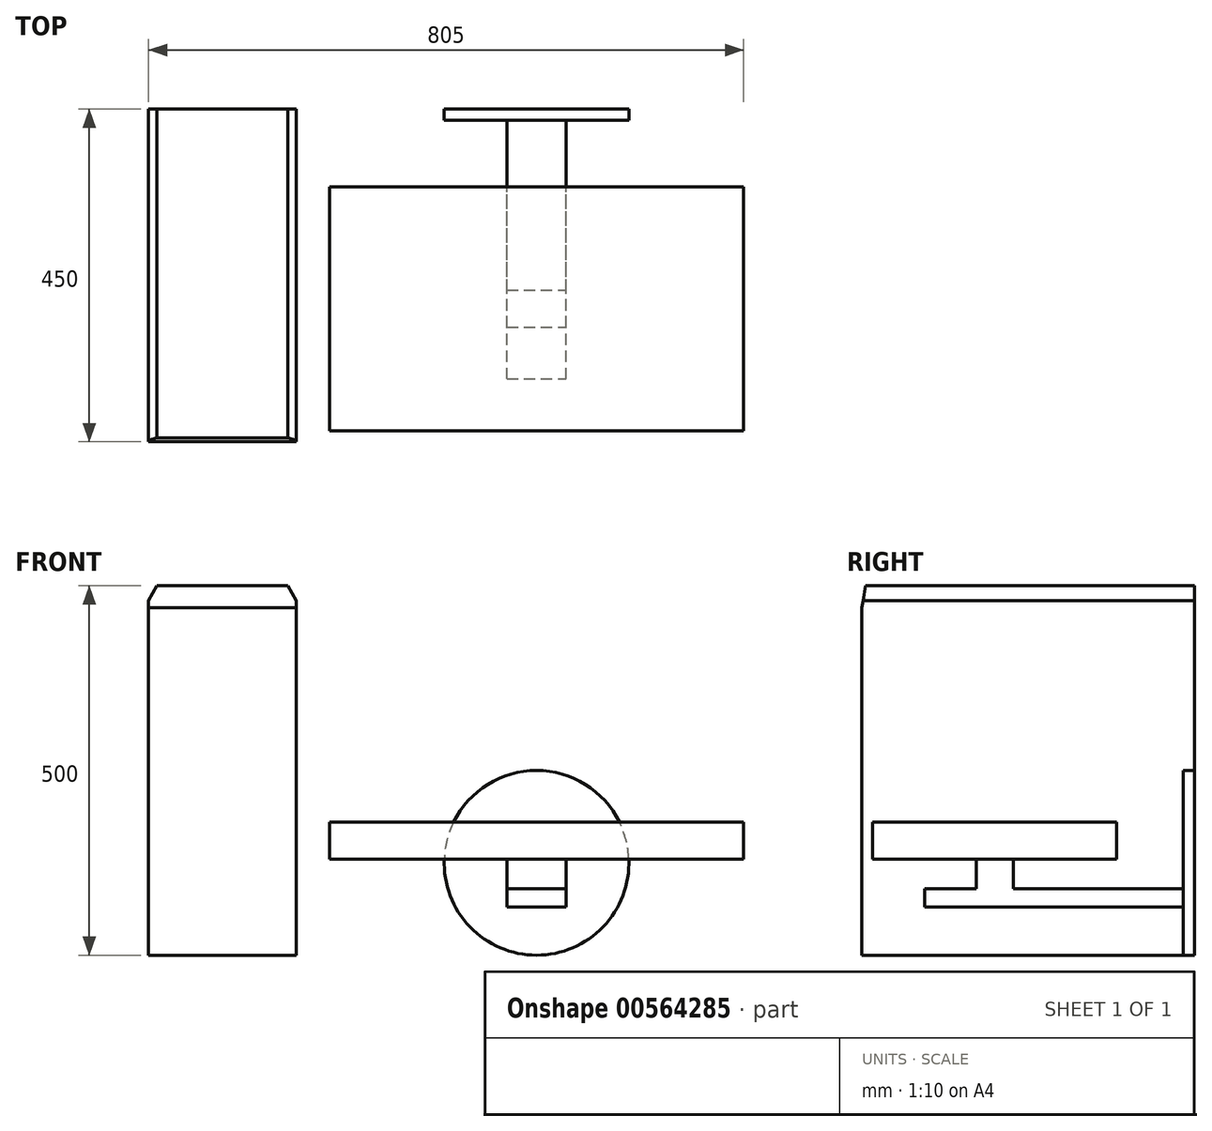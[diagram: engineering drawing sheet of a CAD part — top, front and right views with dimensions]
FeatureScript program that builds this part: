
annotation { "Feature Type Name" : "Feature", "Feature Type Description" : "" }
export const myFeature = defineFeature(function(context is Context, id is Id, definition is map)
    precondition{}
    {
        {
            var Q0;
            Q0=qCreatedBy(makeId("Front.planeOp"),FACE);
            var sketch = newSketch(context, id + "F0", { "sketchPlane" : qUnion([Q0])});
            skLineSegment(sketch, "E0.bottom", {"start": v(-101.54, 321.22) * mm, "end": v(98.46, 321.22) * mm});
            skLineSegment(sketch, "E0.top", {"start": v(-101.54, -178.78) * mm, "end": v(98.46, -178.78) * mm});
            skLineSegment(sketch, "E0.left", {"start": v(-101.54, 321.22) * mm, "end": v(-101.54, -178.78) * mm});
            skLineSegment(sketch, "E0.right", {"start": v(98.46, 321.22) * mm, "end": v(98.46, -178.78) * mm});
            skSolve(sketch);
        }
        {
            var Q0;
            Q0=makeQuery(id+"F0.imprint","IMPRINT",FACE,{"disambiguationData":[TD([[makeQuery(id+"F0.imprint","IMPRINT",EDGE,{"derivedFrom":sQuery(id+"F0.wireOp",EDGE,"E0.bottom")}),-1.0]])]});
            extrude(context, id + "F1", {"entities" : qUnion([Q0]), "depth" : 450 * mm, "offsetDistance" : 25 * mm});
        }
        {
            var Q0;
            Q0=qCreatedBy(makeId("Front.planeOp"),FACE);
            var sketch = newSketch(context, id + "F2", { "sketchPlane" : qUnion([Q0])});
            skCircle(sketch, "E1", {"center": v(423.46, -53.78) * mm, "radius": 125 * mm});
            skSolve(sketch);
        }
        {
            var Q0;
            Q0=makeQuery(id+"F2.imprint","IMPRINT",FACE,{"disambiguationData":[TD([[makeQuery(id+"F2.imprint","IMPRINT",EDGE,{"derivedFrom":sQuery(id+"F2.wireOp",EDGE,"E1")}),1.0]])]});
            extrude(context, id + "F3", {"entities" : qUnion([Q0]), "depth" : 15 * mm, "offsetDistance" : 25 * mm});
        }
        {
            var Q0;
            Q0=makeQuery(id+"F3.opExtrude","CAP_FACE",FACE,{"disambiguationData":[OSD([sQuery(id+"F2.wireOp",EDGE,"E1")])],"isStart":false});
            var sketch = newSketch(context, id + "F4", { "sketchPlane" : qUnion([Q0])});
            skLineSegment(sketch, "E2.bottom", {"start": v(383.46, -88.78) * mm, "end": v(463.46, -88.78) * mm});
            skLineSegment(sketch, "E2.top", {"start": v(383.46, -113.78) * mm, "end": v(463.46, -113.78) * mm});
            skLineSegment(sketch, "E2.left", {"start": v(383.46, -88.78) * mm, "end": v(383.46, -113.78) * mm});
            skLineSegment(sketch, "E2.right", {"start": v(463.46, -88.78) * mm, "end": v(463.46, -113.78) * mm});
            skSolve(sketch);
        }
        {
            var Q0;
            Q0=makeQuery(id+"F4.imprint","IMPRINT",FACE,{"disambiguationData":[TD([[makeQuery(id+"F4.imprint","IMPRINT",EDGE,{"derivedFrom":sQuery(id+"F4.wireOp",EDGE,"E2.bottom")}),-1.0]])]});
            extrude(context, id + "F5", {"entities" : qUnion([Q0]), "operationType" : NewBodyOperationType.ADD, "depth" : 350 * mm, "offsetDistance" : 25 * mm});
        }
        {
            var Q0;
            Q0=makeQuery(id+"F5.opExtrude","SWEPT_FACE",FACE,{"disambiguationData":[OSD([sQuery(id+"F4.wireOp",EDGE,"E2.bottom")])]});
            var sketch = newSketch(context, id + "F6", { "sketchPlane" : qUnion([Q0])});
            skLineSegment(sketch, "E3.bottom", {"start": v(383.46, -245) * mm, "end": v(463.46, -245) * mm});
            skLineSegment(sketch, "E3.top", {"start": v(383.46, -295) * mm, "end": v(463.46, -295) * mm});
            skLineSegment(sketch, "E3.left", {"start": v(383.46, -245) * mm, "end": v(383.46, -295) * mm});
            skLineSegment(sketch, "E3.right", {"start": v(463.46, -245) * mm, "end": v(463.46, -295) * mm});
            skSolve(sketch);
        }
        {
            var Q0;
            Q0=makeQuery(id+"F6.imprint","IMPRINT",FACE,{"disambiguationData":[TD([[makeQuery(id+"F6.imprint","IMPRINT",EDGE,{"derivedFrom":sQuery(id+"F6.wireOp",EDGE,"E3.bottom")}),-1.0]])]});
            extrude(context, id + "F7", {"entities" : qUnion([Q0]), "operationType" : NewBodyOperationType.ADD, "depth" : 40 * mm, "offsetDistance" : 25 * mm});
        }
        {
            var Q0;
            Q0=makeQuery(id+"F7.opExtrude","CAP_FACE",FACE,{"disambiguationData":[OSD([sQuery(id+"F6.wireOp",EDGE,"E3.bottom"),sQuery(id+"F6.wireOp",EDGE,"E3.top"),sQuery(id+"F6.wireOp",EDGE,"E3.left"),sQuery(id+"F6.wireOp",EDGE,"E3.right")])],"isStart":false});
            var sketch = newSketch(context, id + "F8", { "sketchPlane" : qUnion([Q0])});
            skLineSegment(sketch, "E4.bottom", {"start": v(143.46, -105) * mm, "end": v(703.46, -105) * mm});
            skLineSegment(sketch, "E4.top", {"start": v(143.46, -435) * mm, "end": v(703.46, -435) * mm});
            skLineSegment(sketch, "E4.left", {"start": v(143.46, -105) * mm, "end": v(143.46, -435) * mm});
            skLineSegment(sketch, "E4.right", {"start": v(703.46, -105) * mm, "end": v(703.46, -435) * mm});
            skSolve(sketch);
        }
        {
            var Q0;
            Q0 = qSketchRegion(id + "F8", true);
            extrude(context, id + "F9", {"entities" : qUnion([Q0]), "operationType" : NewBodyOperationType.ADD, "depth" : 50 * mm, "offsetDistance" : 25 * mm});
        }
        {
            var Q0;
            Q0=makeQuery(id+"F1.opExtrude","SWEPT_EDGE",EDGE,{"disambiguationData":[OSD([sQuery(id+"F0.wireOp",EDGE,"E0.bottom"),sQuery(id+"F0.wireOp",EDGE,"E0.right")])]});
            var Q1;
            Q1=makeQuery(id+"F1.opExtrude","SWEPT_EDGE",EDGE,{"disambiguationData":[OSD([sQuery(id+"F0.wireOp",EDGE,"E0.bottom"),sQuery(id+"F0.wireOp",EDGE,"E0.left")])]});
            chamfer(context, id + "F10", {"entities" : qUnion([Q0, Q1]), "chamferType" : ChamferType.OFFSET_ANGLE, "width" : 20 * mm, "oppositeDirection" : true, "angle" : 30 * degree, "tangentPropagation" : true});
        }
        {
            var Q0;
            Q0=makeQuery(id+"F1.opExtrude","CAP_EDGE",EDGE,{"disambiguationData":[OSD([sQuery(id+"F0.wireOp",EDGE,"E0.bottom")])],"isStart":false});
            chamfer(context, id + "F11", {"entities" : qUnion([Q0]), "chamferType" : ChamferType.OFFSET_ANGLE, "width" : 30 * mm, "oppositeDirection" : true, "angle" : 10 * degree, "tangentPropagation" : true});
        }
    });
